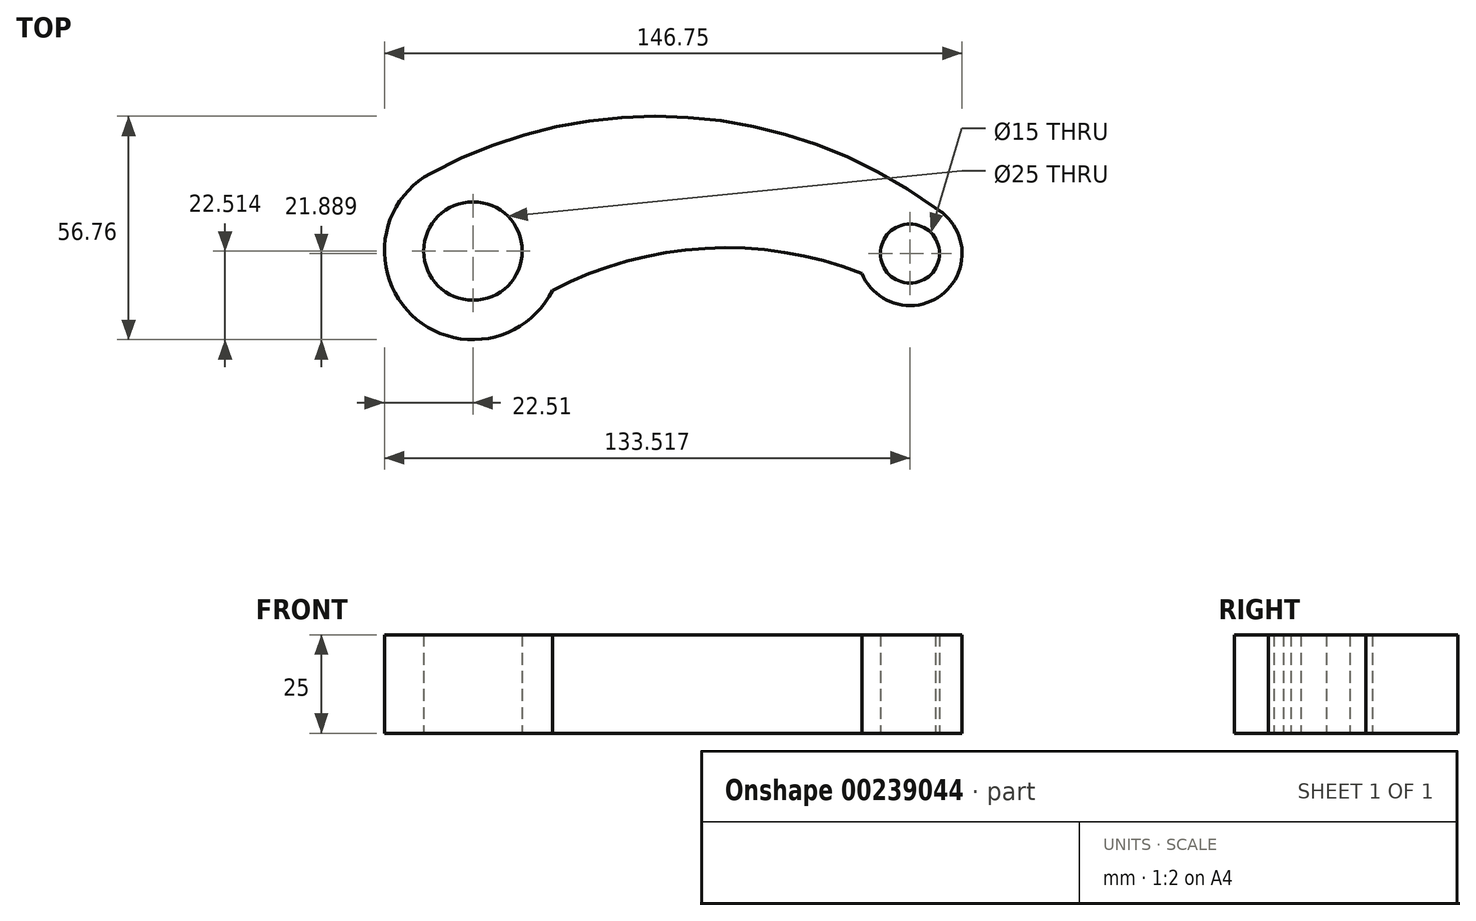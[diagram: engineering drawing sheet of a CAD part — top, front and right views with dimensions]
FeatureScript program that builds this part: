
annotation { "Feature Type Name" : "Feature", "Feature Type Description" : "" }
export const myFeature = defineFeature(function(context is Context, id is Id, definition is map)
    precondition{}
    {
        {
            var Q0;
            Q0=qCreatedBy(makeId("Top.planeOp"),FACE);
            var sketch = newSketch(context, id + "F0", { "sketchPlane" : qUnion([Q0])});
            skLineSegment(sketch, "E0", {"start": v(-85.43, -8.19) * mm, "end": v(-72.93, -8.26) * mm});
            skCircle(sketch, "E1", {"center": v(-85.43, -8.19) * mm, "radius": 12.5 * mm});
            skCircle(sketch, "E2", {"center": v(25.58, -8.81) * mm, "radius": 7.5 * mm});
            skLineSegment(sketch, "E3.trimOffspring", {"start": v(18.08, -8.77) * mm, "end": v(25.58, -8.81) * mm});
            skLineSegment(sketch, "E4", {"start": v(-85.43, -8.19) * mm, "end": v(-85.94, -98.18) * mm});
            skLineSegment(sketch, "E5", {"start": v(-85.94, -98.18) * mm, "end": v(-25.94, -98.18) * mm});
            skArc(sketch, "E6", {"start": v(-63.93, -14.87) * mm, "mid": v(-99.68, -25.62) * mm, "end": v(-96.26, 11.55) * mm});
            skArc(sketch, "E7", {"start": v(13.34, -13.84) * mm, "mid": v(34.35, -18.72) * mm, "end": v(32.05, 2.73) * mm});
            skArc(sketch, "E8", {"start": v(32.05, 2.73) * mm, "mid": v(-30.82, 25.78) * mm, "end": v(-96.26, 11.55) * mm});
            skArc(sketch, "E9", {"start": v(13.34, -13.84) * mm, "mid": v(-26.45, -7.5) * mm, "end": v(-65.28, -18.22) * mm});
            skSolve(sketch);
        }
        {
            var Q0;
            Q0=makeQuery(id+"F0.imprint","IMPRINT",FACE,{"disambiguationData":[TD([[makeQuery(id+"F0.imprint","IMPRINT",EDGE,{"derivedFrom":sQuery(id+"F0.wireOp",EDGE,"E2")}),-1.0]])]});
            extrude(context, id + "F1", {"entities" : qUnion([Q0]), "depth" : 25 * mm});
        }
    });
